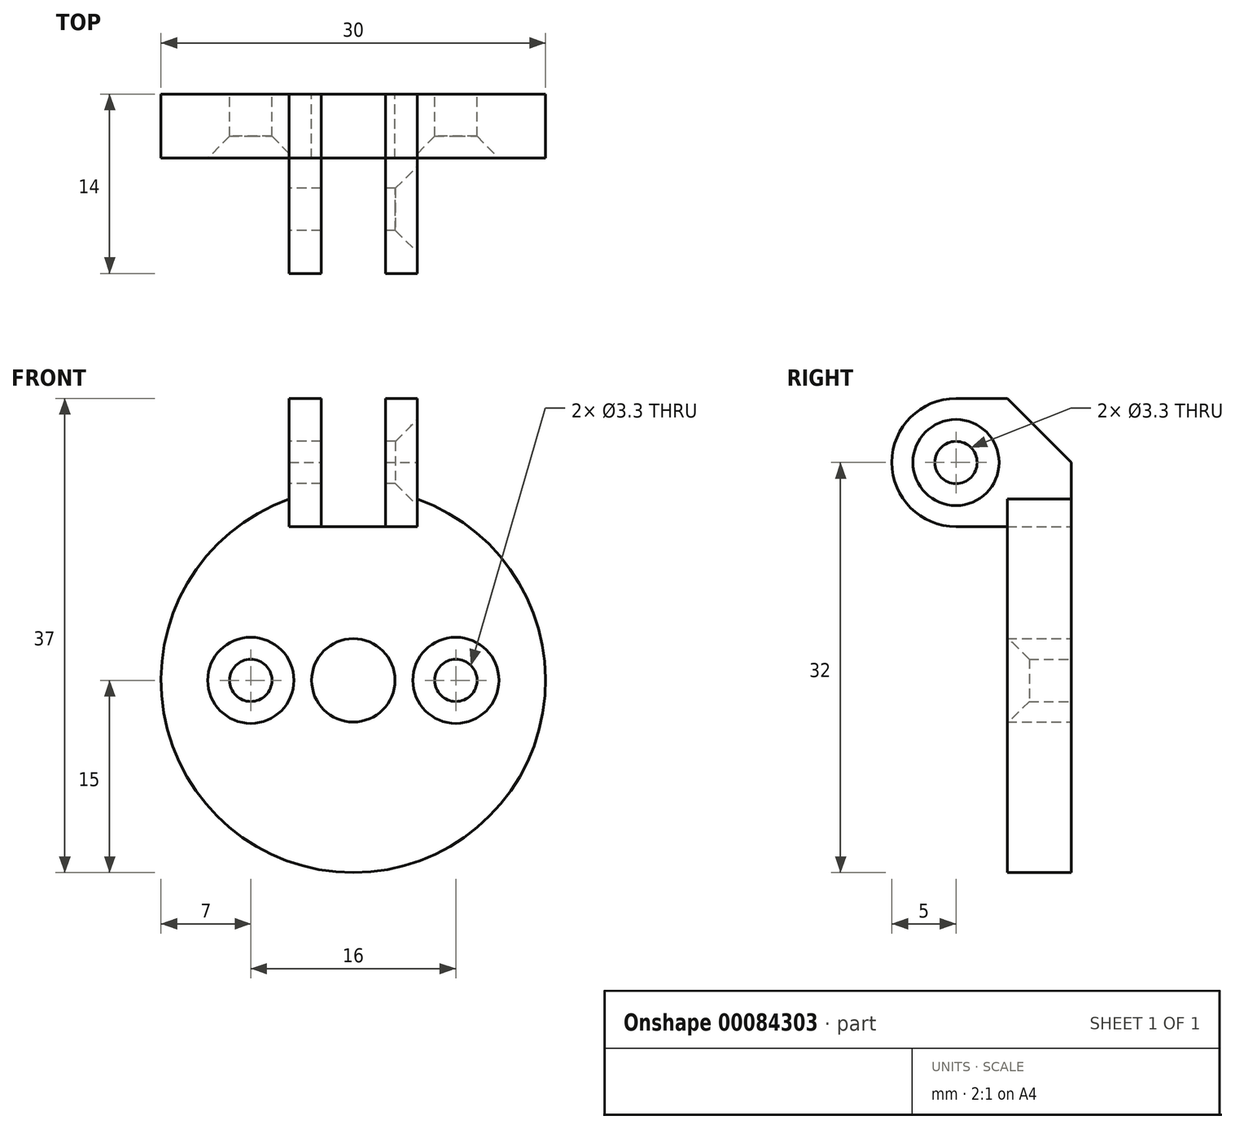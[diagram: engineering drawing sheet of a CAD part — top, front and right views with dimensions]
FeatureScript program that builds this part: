
annotation { "Feature Type Name" : "Feature", "Feature Type Description" : "" }
export const myFeature = defineFeature(function(context is Context, id is Id, definition is map)
    precondition{}
    {
        {
            var Q0;
            Q0=qCreatedBy(makeId("Front.planeOp"),FACE);
            var sketch = newSketch(context, id + "F0", { "sketchPlane" : qUnion([Q0])});
            skCircle(sketch, "E0", {"center": v(0, 0) * mm, "radius": 15 * mm});
            skCircle(sketch, "E1", {"center": v(0, 0) * mm, "radius": 3.25 * mm});
            skSolve(sketch);
        }
        {
            var Q0;
            Q0 = qSketchRegion(id + "F0", true);
            extrude(context, id + "F1", {"entities" : qUnion([Q0]), "depth" : 5 * mm});
        }
        {
            var Q0;
            Q0=qCreatedBy(makeId("Right.planeOp"),FACE);
            var sketch = newSketch(context, id + "F2", { "sketchPlane" : qUnion([Q0])});
            skLineSegment(sketch, "E2", {"start": v(0, 12) * mm, "end": v(-9, 12) * mm});
            skLineSegment(sketch, "E3", {"start": v(-9, 22) * mm, "end": v(0, 22) * mm});
            skLineSegment(sketch, "E4", {"start": v(0, 22) * mm, "end": v(0, 12) * mm});
            skArc(sketch, "E5", {"start": v(-9, 22) * mm, "mid": v(-14, 17) * mm, "end": v(-9, 12) * mm});
            skSolve(sketch);
        }
        {
            var Q0;
            Q0 = qSketchRegion(id + "F2", true);
            extrude(context, id + "F3", {"entities" : qUnion([Q0]), "operationType" : NewBodyOperationType.ADD, "depth" : 10 * mm, "symmetric" : true});
        }
        {
            var Q0;
            Q0=makeQuery(id+"F3.boolean.opBoolean","MERGE",FACE,{"derivedFrom":[makeQuery(id+"F1.opExtrude","CAP_FACE",FACE,{"disambiguationData":[OSD([sQuery(id+"F0.wireOp",EDGE,"E0"),sQuery(id+"F0.wireOp",EDGE,"E1")])],"isStart":true}),makeQuery(id+"F3.opExtrude","SWEPT_FACE",FACE,{"disambiguationData":[OSD([sQuery(id+"F2.wireOp",EDGE,"E4")])]})]});
            var sketch = newSketch(context, id + "F4", { "sketchPlane" : qUnion([Q0])});
            skLineSegment(sketch, "E6", {"start": v(0, 22) * mm, "end": v(-2.5, 22) * mm});
            skLineSegment(sketch, "E7", {"start": v(-2.5, 22) * mm, "end": v(-2.5, 12) * mm});
            skLineSegment(sketch, "E8", {"start": v(-2.5, 12) * mm, "end": v(0, 12) * mm});
            skLineSegment(sketch, "E9", {"start": v(0, 12) * mm, "end": v(0, 22) * mm, "construction": true});
            skLineSegment(sketch, "E10", {"start": v(0, 22) * mm, "end": v(2.5, 22) * mm});
            skLineSegment(sketch, "E11", {"start": v(2.5, 22) * mm, "end": v(2.5, 12) * mm});
            skLineSegment(sketch, "E12", {"start": v(2.5, 12) * mm, "end": v(0, 12) * mm});
            skSolve(sketch);
        }
        {
            var Q0;
            Q0 = qSketchRegion(id + "F4", true);
            extrude(context, id + "F5", {"entities" : qUnion([Q0]), "operationType" : NewBodyOperationType.REMOVE, "endBound" : BoundingType.THROUGH_ALL, "oppositeDirection" : true, "depth" : 25 * mm});
        }
        {
            var Q0;
            Q0=makeQuery(id+"F3.opExtrude","CAP_FACE",FACE,{"disambiguationData":[OSD([sQuery(id+"F2.wireOp",EDGE,"E2"),sQuery(id+"F2.wireOp",EDGE,"E3"),sQuery(id+"F2.wireOp",EDGE,"E4"),sQuery(id+"F2.wireOp",EDGE,"E5")])],"isStart":false});
            var sketch = newSketch(context, id + "F6", { "sketchPlane" : qUnion([Q0])});
            skPoint(sketch, "E13", {"position": v(-9, 17) * mm});
            skSolve(sketch);
        }
        {
            var Q0;
            Q0=sQuery(id+"F6.wireOp",VERTEX,"E13");
            var Q1;
            Q1=makeQuery(id+"F1.opExtrude","SWEPT_BODY",BODY,{"disambiguationData":[OSD([sQuery(id+"F0.wireOp",EDGE,"E0"),sQuery(id+"F0.wireOp",EDGE,"E1")])]});
            hole(context, id + "F7", {"style" : HoleStyle.C_SINK, "endStyle" : HoleEndStyle.THROUGH, "standardTappedOrClearance" : lookupTablePath({ "standard" : "ISO", "fit" : "Normal", "size" : "M3", "type" : "Clearance" }), "standardBlindInLast" : lookupTablePath({ "fit" : "Standard", "standard" : "ISO", "size" : "M3", "type" : "Clearance" }), "holeDiameter" : 3.3 * mm, "cSinkDiameter" : 6.72 * mm, "cSinkAngle" : 90 * degree, "locations" : qUnion([Q0]), "scope" : qUnion([Q1]), "isTappedThrough" : true});
        }
        {
            var Q0;
            Q0=makeQuery(id+"F1.opExtrude","CAP_FACE",FACE,{"disambiguationData":[OSD([sQuery(id+"F0.wireOp",EDGE,"E0"),sQuery(id+"F0.wireOp",EDGE,"E1")])],"isStart":false});
            var sketch = newSketch(context, id + "F8", { "sketchPlane" : qUnion([Q0])});
            skPoint(sketch, "E14", {"position": v(-8, 0) * mm});
            skPoint(sketch, "E15", {"position": v(8, 0) * mm});
            skSolve(sketch);
        }
        {
            var Q0;
            Q0=sQuery(id+"F8.wireOp",VERTEX,"E14");
            var Q1;
            Q1=sQuery(id+"F8.wireOp",VERTEX,"E15");
            var Q2;
            Q2=makeQuery(id+"F1.opExtrude","SWEPT_BODY",BODY,{"disambiguationData":[OSD([sQuery(id+"F0.wireOp",EDGE,"E0"),sQuery(id+"F0.wireOp",EDGE,"E1")])]});
            hole(context, id + "F9", {"style" : HoleStyle.C_SINK, "endStyle" : HoleEndStyle.THROUGH, "standardTappedOrClearance" : lookupTablePath({ "standard" : "ISO", "fit" : "Normal", "size" : "M3", "type" : "Clearance" }), "standardBlindInLast" : lookupTablePath({ "fit" : "Standard", "standard" : "ISO", "size" : "M3", "type" : "Clearance" }), "holeDiameter" : 3.3 * mm, "cSinkDiameter" : 6.72 * mm, "cSinkAngle" : 90 * degree, "locations" : qUnion([Q0, Q1]), "scope" : qUnion([Q2]), "isTappedThrough" : true});
        }
        {
            var Q0;
            {var subQ0=sQuery(id+"F2.wireOp",EDGE,"E4");var subQ1=sQuery(id+"F2.wireOp",EDGE,"E3");Q0=makeQuery(id+"F5.boolean.opBoolean","SPLIT",EDGE,{"disambiguationData":[TD([makeQuery(id+"F5.opExtrude","SWEPT_FACE",FACE,{"disambiguationData":[OSD([sQuery(id+"F4.wireOp",EDGE,"E11")])]})])],"derivedFrom":makeQuery(id+"F3.opExtrude","SWEPT_EDGE",EDGE,{"disambiguationData":[OSD([subQ1,subQ0])]})});}
            var Q1;
            {var subQ0=sQuery(id+"F2.wireOp",EDGE,"E4");var subQ1=sQuery(id+"F2.wireOp",EDGE,"E3");Q1=makeQuery(id+"F5.boolean.opBoolean","SPLIT",EDGE,{"disambiguationData":[TD([makeQuery(id+"F5.opExtrude","SWEPT_FACE",FACE,{"disambiguationData":[OSD([sQuery(id+"F4.wireOp",EDGE,"E7")])]})])],"derivedFrom":makeQuery(id+"F3.opExtrude","SWEPT_EDGE",EDGE,{"disambiguationData":[OSD([subQ1,subQ0])]})});}
            var Q2;
            {var subQ0=sQuery(id+"F2.wireOp",EDGE,"E4");var subQ1=sQuery(id+"F2.wireOp",EDGE,"E3");Q2=makeQuery(id+"F4xup2BdCmlQ2pm_1.2.F5.boolean.opBoolean","SPLIT",EDGE,{"disambiguationData":[TD([makeQuery(id+"F4xup2BdCmlQ2pm_1.2.F5.opExtrude","SWEPT_FACE",FACE,{"disambiguationData":[OSD([sQuery(id+"F4.wireOp",EDGE,"E11")])]})])],"derivedFrom":makeQuery(id+"F4xup2BdCmlQ2pm_1.2.F3.opExtrude","SWEPT_EDGE",EDGE,{"disambiguationData":[OSD([subQ1,subQ0])]})});}
            var Q3;
            {var subQ0=sQuery(id+"F2.wireOp",EDGE,"E4");var subQ1=sQuery(id+"F2.wireOp",EDGE,"E3");Q3=makeQuery(id+"F4xup2BdCmlQ2pm_1.2.F5.boolean.opBoolean","SPLIT",EDGE,{"disambiguationData":[TD([makeQuery(id+"F4xup2BdCmlQ2pm_1.2.F5.opExtrude","SWEPT_FACE",FACE,{"disambiguationData":[OSD([sQuery(id+"F4.wireOp",EDGE,"E7")])]})])],"derivedFrom":makeQuery(id+"F4xup2BdCmlQ2pm_1.2.F3.opExtrude","SWEPT_EDGE",EDGE,{"disambiguationData":[OSD([subQ1,subQ0])]})});}
            var Q4;
            {var subQ0=sQuery(id+"F2.wireOp",EDGE,"E3");var subQ1=sQuery(id+"F2.wireOp",EDGE,"E4");Q4=makeQuery(id+"F4xup2BdCmlQ2pm_1.1.F5.boolean.opBoolean","SPLIT",EDGE,{"disambiguationData":[TD([makeQuery(id+"F4xup2BdCmlQ2pm_1.1.F5.opExtrude","SWEPT_FACE",FACE,{"disambiguationData":[OSD([sQuery(id+"F4.wireOp",EDGE,"E7")])]})])],"derivedFrom":makeQuery(id+"F4xup2BdCmlQ2pm_1.1.F3.opExtrude","SWEPT_EDGE",EDGE,{"disambiguationData":[OSD([subQ0,subQ1])]})});}
            var Q5;
            {var subQ0=sQuery(id+"F2.wireOp",EDGE,"E3");var subQ1=sQuery(id+"F2.wireOp",EDGE,"E4");Q5=makeQuery(id+"F4xup2BdCmlQ2pm_1.1.F5.boolean.opBoolean","SPLIT",EDGE,{"disambiguationData":[TD([makeQuery(id+"F4xup2BdCmlQ2pm_1.1.F5.opExtrude","SWEPT_FACE",FACE,{"disambiguationData":[OSD([sQuery(id+"F4.wireOp",EDGE,"E11")])]})])],"derivedFrom":makeQuery(id+"F4xup2BdCmlQ2pm_1.1.F3.opExtrude","SWEPT_EDGE",EDGE,{"disambiguationData":[OSD([subQ0,subQ1])]})});}
            chamfer(context, id + "F10", {"entities" : qUnion([Q0, Q1, Q2, Q3, Q4, Q5]), "width" : 5 * mm, "tangentPropagation" : true});
        }
    });
